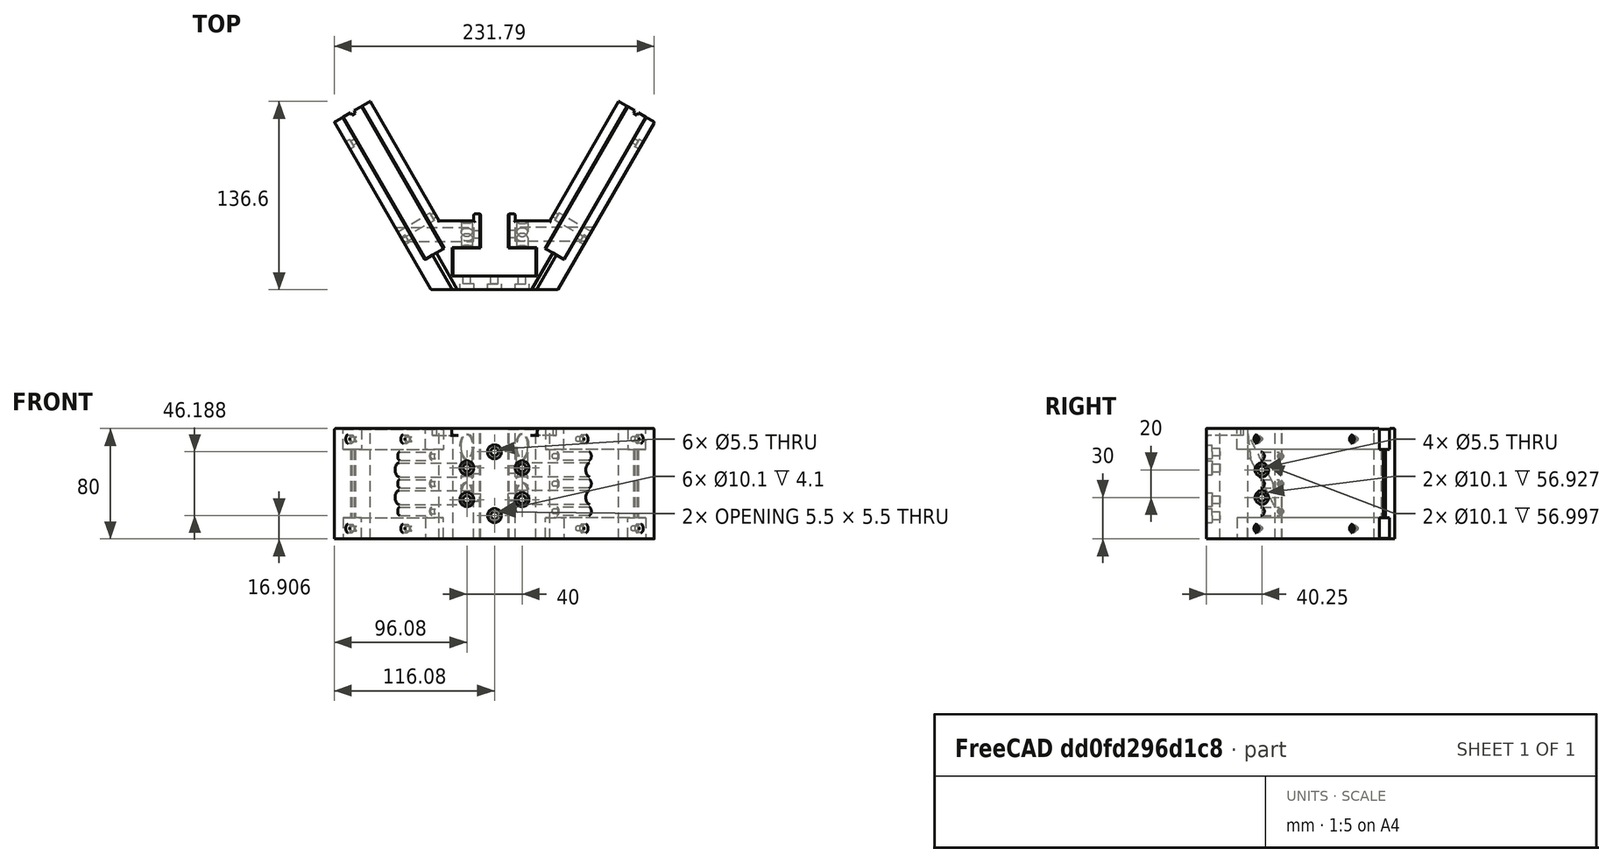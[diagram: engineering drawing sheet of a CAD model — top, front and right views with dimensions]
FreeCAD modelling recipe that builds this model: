
FCSTD DOCUMENT  (FreeCAD 2022.407R26244 +4693 (Git))
Label: As3BottomCorner-M3x10
License: All rights reserved
LicenseURL: http://en.wikipedia.org/wiki/All_rights_reserved
objects: Part::FeaturePython×13, App::FeaturePython×2, Part::Feature×1
note: 13 computed .brp shape members not serialized (recipe doc carries the construction recipe); baked Part::Feature solids carry a one-line shape summary decoded from their .brp

FEATURE [App::FeaturePython] Constraints  # WARN: FeaturePython — macro-defined, semantics opaque (R4)
  TreeRank = 0
  _LinkVersion = 1
  _Version = 1
FEATURE [Part::Feature] ShapeCopy  label="BottomCornerM3x10"
  TreeRank = 44
  shape: bbox 232.2 x 136.6 x 80 mm, 177 faces (baked)
FEATURE [Part::FeaturePython] Parts  # WARN: FeaturePython — macro-defined, semantics opaque (R4)
  Group = -> [ShapeCopy]
  GroupMode = 0
  TreeRank = 0
  _LinkVersion = 1
FEATURE [Part::FeaturePython] Assembly  label="As3BottomCorner-M3x10"  # WARN: FeaturePython — macro-defined, semantics opaque (R4)
  AutoRelax = true
  BuildShape = 0
  Freeze = false
  Group = -> [Constraints,Elements,Parts]
  TreeRank = 0
  Verbose = false
  _LinkVersion = 1
  _SolverType = 1
  _Version = 1
FEATURE [App::FeaturePython] Elements  # WARN: FeaturePython — macro-defined, semantics opaque (R4)
  Group = -> [Element,Element001,Element002,Element003,Element004,Element005,Element006,Element007,Element008,Element009,Element010]
  TreeRank = 0
  _LinkVersion = 1
FEATURE [Part::FeaturePython] Element  label="FaceRef"  # link proxy (typed FeaturePython)
  Detach = false
  LinkTransform = true
  LinkedObject = -> ShapeCopy [Face37]
  TreeRank = 0
  _LinkVersion = 1
  _Parent = -> Elements
FEATURE [Part::FeaturePython] Element001  label="AppuiPoteau1"  # link proxy (typed FeaturePython)
  Detach = false
  LinkTransform = true
  LinkedObject = -> ShapeCopy [Face9]
  TreeRank = 0
  _LinkVersion = 1
  _Parent = -> Elements
FEATURE [Part::FeaturePython] Element002  label="AppuiPoteau2"  # link proxy (typed FeaturePython)
  Detach = false
  LinkTransform = true
  LinkedObject = -> ShapeCopy [Face35]
  TreeRank = 0
  _LinkVersion = 1
  _Parent = -> Elements
FEATURE [Part::FeaturePython] Element003  label="AppuiTrav1v"  # link proxy (typed FeaturePython)
  Detach = false
  LinkTransform = true
  LinkedObject = -> ShapeCopy [Face51]
  TreeRank = 0
  _LinkVersion = 1
  _Parent = -> Elements
FEATURE [Part::FeaturePython] Element004  label="AppuiTrav1h"  # link proxy (typed FeaturePython)
  Detach = false
  LinkTransform = true
  LinkedObject = -> ShapeCopy [Face49]
  TreeRank = 0
  _LinkVersion = 1
  _Parent = -> Elements
FEATURE [Part::FeaturePython] Element005  label="AppuiTrav2h"  # link proxy (typed FeaturePython)
  Detach = false
  LinkTransform = true
  LinkedObject = -> ShapeCopy [Face45]
  TreeRank = 0
  _LinkVersion = 1
  _Parent = -> Elements
FEATURE [Part::FeaturePython] Element006  label="AppuiTrv2v"  # link proxy (typed FeaturePython)
  Detach = false
  LinkTransform = true
  LinkedObject = -> ShapeCopy [Face79]
  TreeRank = 0
  _LinkVersion = 1
  _Parent = -> Elements
FEATURE [Part::FeaturePython] Element007  label="ExtremRain1"  # link proxy (typed FeaturePython)
  Detach = false
  LinkTransform = true
  LinkedObject = -> ShapeCopy [Face12]
  TreeRank = 0
  _LinkVersion = 1
  _Parent = -> Elements
FEATURE [Part::FeaturePython] Element008  label="ExtremRain2"  # link proxy (typed FeaturePython)
  Detach = false
  LinkTransform = true
  LinkedObject = -> ShapeCopy [Face25]
  TreeRank = 0
  _LinkVersion = 1
  _Parent = -> Elements
FEATURE [Part::FeaturePython] Element009  label="FixM1"  # link proxy (typed FeaturePython)
  Detach = false
  LinkTransform = true
  LinkedObject = -> ShapeCopy [Edge168]
  TreeRank = 0
  _LinkVersion = 1
  _Parent = -> Elements
FEATURE [Part::FeaturePython] Element010  label="FixM2"  # link proxy (typed FeaturePython)
  Detach = false
  LinkTransform = true
  LinkedObject = -> ShapeCopy [Edge287]
  TreeRank = 0
  _LinkVersion = 1
  _Parent = -> Elements
